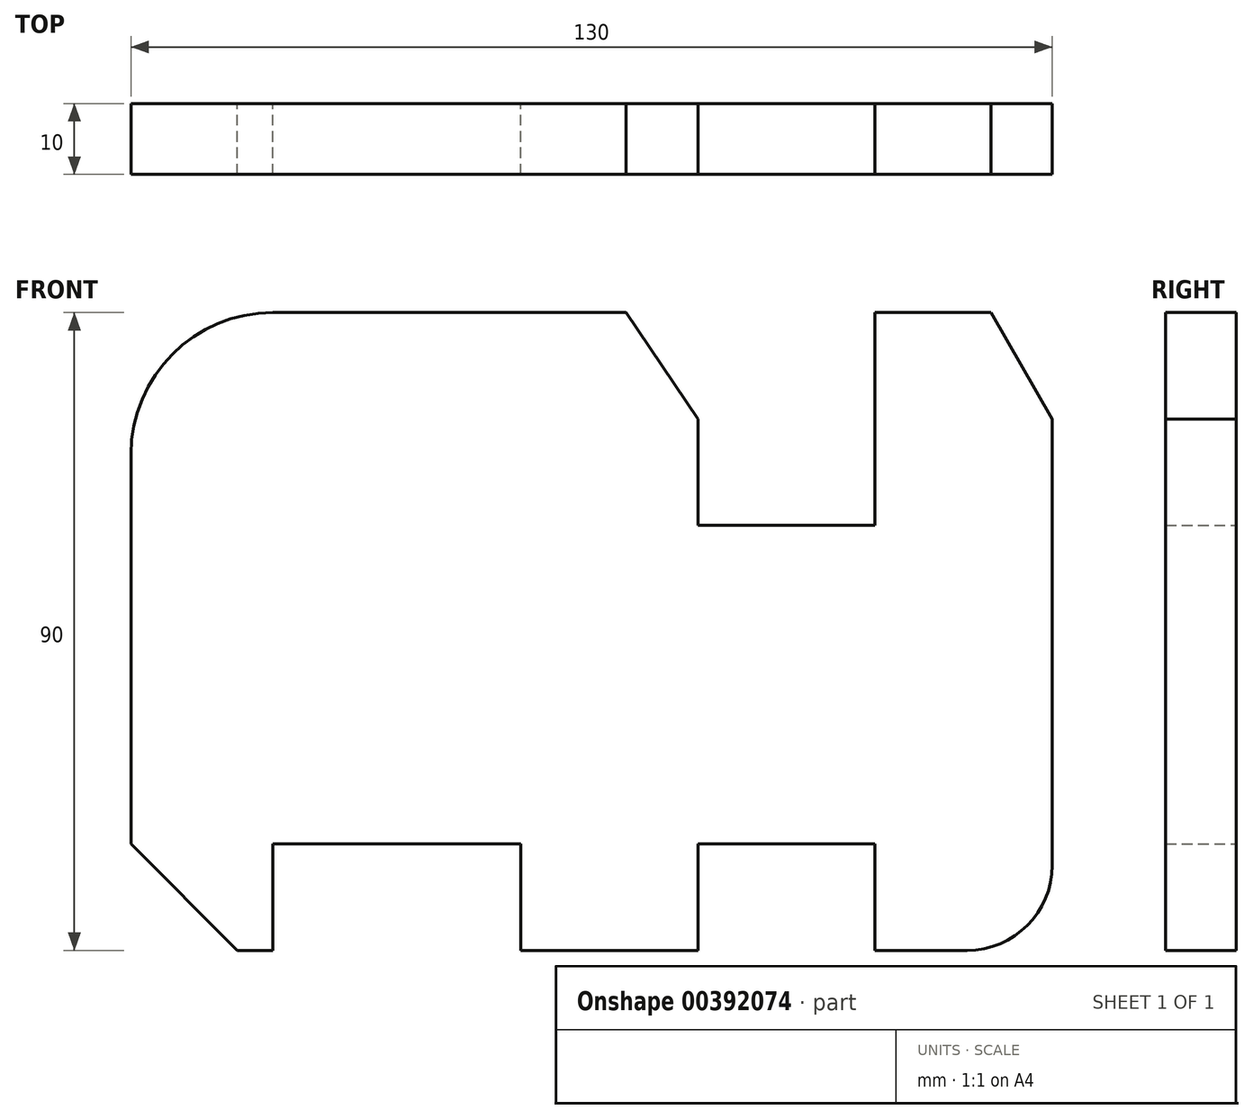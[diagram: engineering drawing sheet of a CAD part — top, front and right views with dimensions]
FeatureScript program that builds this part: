
annotation { "Feature Type Name" : "Feature", "Feature Type Description" : "" }
export const myFeature = defineFeature(function(context is Context, id is Id, definition is map)
    precondition{}
    {
        {
            var Q0;
            Q0=qCreatedBy(makeId("Front.planeOp"),FACE);
            var sketch = newSketch(context, id + "F0", { "sketchPlane" : qUnion([Q0])});
            skLineSegment(sketch, "E0.top", {"start": v(20, 90) * mm, "end": v(69.88, 90) * mm});
            skLineSegment(sketch, "E0.left", {"start": v(0, 15) * mm, "end": v(0, 70) * mm});
            skLineSegment(sketch, "E0.right", {"start": v(130, 12) * mm, "end": v(130, 75) * mm});
            skLineSegment(sketch, "E1", {"start": v(20, 15) * mm, "end": v(55, 15) * mm});
            skLineSegment(sketch, "E2", {"start": v(55, 15) * mm, "end": v(55, 0) * mm});
            skLineSegment(sketch, "E3.trimOffspring", {"start": v(55, 0) * mm, "end": v(80, 0) * mm});
            skLineSegment(sketch, "E4", {"start": v(0, 15) * mm, "end": v(15, 0) * mm});
            skPoint(sketch, "E5.visualSharp", {"position": v(0, 90) * mm});
            skArc(sketch, "E5.filletArc", {"start": v(20, 90) * mm, "mid": v(5.86, 84.14) * mm, "end": v(0, 70) * mm});
            skLineSegment(sketch, "E6", {"start": v(69.88, 90) * mm, "end": v(80, 75) * mm});
            skLineSegment(sketch, "E7", {"start": v(80, 75) * mm, "end": v(80, 60) * mm});
            skLineSegment(sketch, "E8", {"start": v(80, 60) * mm, "end": v(105, 60) * mm});
            skLineSegment(sketch, "E9", {"start": v(105, 60) * mm, "end": v(105, 90) * mm});
            skLineSegment(sketch, "E10.trimOffspring", {"start": v(105, 90) * mm, "end": v(121.34, 90) * mm});
            skPoint(sketch, "E11.visualSharp", {"position": v(130, 0) * mm});
            skArc(sketch, "E11.filletArc", {"start": v(118, 0) * mm, "mid": v(126.49, 3.51) * mm, "end": v(130, 12) * mm});
            skLineSegment(sketch, "E12", {"start": v(121.34, 90) * mm, "end": v(130, 75) * mm});
            skLineSegment(sketch, "E13", {"start": v(80, 0) * mm, "end": v(80, 15) * mm});
            skLineSegment(sketch, "E14", {"start": v(80, 15) * mm, "end": v(105, 15) * mm});
            skLineSegment(sketch, "E15", {"start": v(105, 15) * mm, "end": v(105, 0) * mm});
            skLineSegment(sketch, "E16.trimOffspring", {"start": v(105, 0) * mm, "end": v(118, 0) * mm});
            skPoint(sketch, "E17.orphan", {"position": v(0, 0) * mm});
            skLineSegment(sketch, "E18", {"start": v(20, 15) * mm, "end": v(20, 0) * mm});
            skLineSegment(sketch, "E19", {"start": v(20, 0) * mm, "end": v(15, 0) * mm});
            skSolve(sketch);
        }
        {
            var Q0;
            Q0 = qSketchRegion(id + "F0", true);
            extrude(context, id + "F1", {"entities" : qUnion([Q0]), "depth" : 10 * mm});
        }
    });
